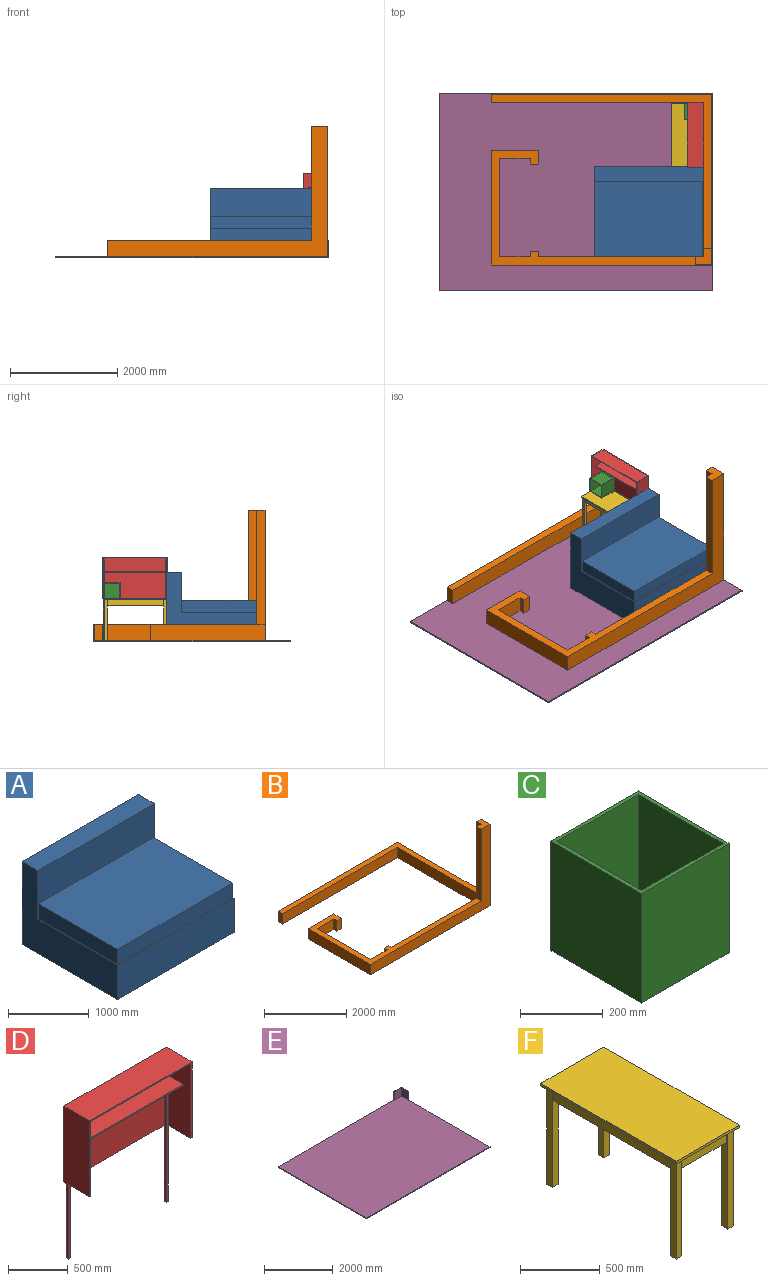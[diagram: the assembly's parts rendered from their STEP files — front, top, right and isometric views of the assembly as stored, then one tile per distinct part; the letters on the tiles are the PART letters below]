
ASSEMBLY  parts=6 mates=12
PART A: 12 faces, bbox 2038.4x1676.4x1257.3 mm
  f0: plane 1676.4x1257.3mm, normal (-1,0,0), area 1078707.5mm2, adj f1,f2,f3,f5,f6,f7
  f1: plane 2038.35x520.7mm, normal (0,-1,0), area 1061368.8mm2, adj f0,f4,f5,f6
  f2: plane 2038.35x279.4mm, normal (0,0,1), area 569515mm2, adj f0,f3,f4,f7
  f3: plane 2038.35x1257.3mm, normal (0,1,0), area 2562817.5mm2, adj f0,f2,f4,f5
  f4: plane 1676.4x1257.3mm, normal (1,0,0), area 1078707.5mm2, adj f1,f2,f3,f5,f6,f7
  f5: plane 2038.35x1676.4mm, normal (0,0,-1), area 3417089.9mm2, adj f0,f1,f3,f4
  f6: plane 2038.35x1397mm, normal (0,0,1), area 61048.3mm2, adj f0,f1,f4,f7,f8,f9,f10
  f7: plane 2038.35x736.6mm, normal (0,-1,0), area 1041288.2mm2, adj f0,f2,f4,f6,f8,f10,f11
  f8: plane 1384.3x228.6mm, normal (-1,0,0), area 316451mm2, adj f6,f7,f9,f11
  f9: plane 2012.95x228.6mm, normal (0,-1,0), area 460160.4mm2, adj f6,f8,f10,f11
  f10: plane 1384.3x228.6mm, normal (1,0,0), area 316451mm2, adj f6,f7,f9,f11
  f11: plane 2012.95x1384.3mm, normal (0,0,1), area 2786526.7mm2, adj f7,f8,f9,f10
PART B: 24 faces, bbox 4102.1x3175x2425.7 mm
  f0: plane 3797.3x2133.6mm, normal (0,0,1), area 1021933.4mm2, adj f1,f2,f3,f4,f5,f6,f7,f8
  f1: plane 304.8x101.6mm, normal (-1,0,0), area 30967.7mm2, adj f0,f2,f18,f20
  f2: plane 571.5x304.8mm, normal (0,1,0), area 174193.2mm2, adj f0,f1,f3,f20
  f3: plane 1828.8x304.8mm, normal (1,0,0), area 557418.2mm2, adj f0,f2,f4,f20
  f4: plane 571.5x304.8mm, normal (0,-1,0), area 174193.2mm2, adj f0,f3,f5,f20
  f5: plane 304.8x101.6mm, normal (-1,0,0), area 30967.7mm2, adj f0,f4,f6,f20
  f6: plane 304.8x152.4mm, normal (0,-1,0), area 46451.5mm2, adj f0,f5,f7,f20
  f7: plane 304.8x254mm, normal (1,0,0), area 77419.2mm2, adj f0,f6,f8,f20
  f8: plane 876.3x304.8mm, normal (0,1,0), area 267096.2mm2, adj f0,f7,f9,f20
  f9: plane 2133.6x304.8mm, normal (-1,0,0), area 650321.3mm2, adj f0,f8,f10,f20
  f10: plane 4102.1x2425.7mm, normal (0,-1,0), area 1896770.4mm2, adj f0,f9,f11,f20,f21,f23
  f11: plane 3175x2425.7mm, normal (1,0,0), area 1614190.3mm2, adj f10,f12,f19,f20,f22,f23
  f12: plane 4102.1x304.8mm, normal (0,1,0), area 1250320.1mm2, adj f11,f13,f19,f20
  f13: plane 304.8x152.4mm, normal (-1,0,0), area 46451.5mm2, adj f12,f14,f19,f20
  f14: plane 3949.7x304.8mm, normal (0,-1,0), area 1203868.6mm2, adj f13,f15,f19,f20
  f15: plane 2870.2x2425.7mm, normal (-1,0,0), area 1198062.1mm2, adj f14,f16,f19,f20,f22,f23
  f16: plane 3073.4x2425.7mm, normal (0,1,0), area 1259997.5mm2, adj f0,f15,f17,f20,f21,f23
  f17: plane 304.8x101.6mm, normal (1,0,0), area 30967.7mm2, adj f0,f16,f18,f20
  f18: plane 304.8x152.4mm, normal (0,1,0), area 46451.5mm2, adj f0,f1,f17,f20
  f19: plane 4102.1x2870.2mm, normal (0,0,1), area 1039352.8mm2, adj f11,f12,f13,f14,f15,f22
  f20: plane 4102.1x3175mm, normal (0,0,-1), area 2130963.5mm2, adj f1,f2,f3,f4,f5,f6,f7,f8
  f21: plane 2120.9x152.4mm, normal (-1,0,0), area 323225.2mm2, adj f0,f10,f16,f23
  f22: plane 2120.9x152.4mm, normal (0,1,0), area 323225.2mm2, adj f11,f15,f19,f23
  f23: plane 304.8x304.8mm, normal (0,0,1), area 69677.3mm2, adj f10,f11,f15,f16,f21,f22
PART C: 11 faces, bbox 298.5x311.2x323.9 mm
  f0: plane 311.15x298.45mm, normal (0,0,-1), area 92862.7mm2, adj f5,f6,f7,f8
  f1: plane 298.45x278.13mm, normal (0,-1,0), area 83007.9mm2, adj f2,f4,f9,f10
  f2: plane 298.45x290.83mm, normal (1,0,0), area 86798.2mm2, adj f1,f3,f9,f10
  f3: plane 298.45x278.13mm, normal (0,1,0), area 83007.9mm2, adj f2,f4,f9,f10
  f4: plane 298.45x290.83mm, normal (-1,0,0), area 86798.2mm2, adj f1,f3,f9,f10
  f5: plane 323.85x298.45mm, normal (0,-1,0), area 96653mm2, adj f0,f6,f8,f9
  f6: plane 323.85x311.15mm, normal (1,0,0), area 100765.9mm2, adj f0,f5,f7,f9
  f7: plane 323.85x298.45mm, normal (0,1,0), area 96653mm2, adj f0,f6,f8,f9
  f8: plane 323.85x311.15mm, normal (-1,0,0), area 100765.9mm2, adj f0,f5,f7,f9
  f9: plane 311.15x298.45mm, normal (0,0,1), area 11974.2mm2, adj f1,f2,f3,f4,f5,f6,f7,f8
  f10: plane 290.83x278.13mm, normal (0,0,1), area 80888.5mm2, adj f1,f2,f3,f4
PART D: 28 faces, bbox 1206.5x304.8x1549.4 mm
  f0: plane 1130.3x254mm, normal (0,-1,0), area 287096.2mm2, adj f13,f17,f23,f25
  f1: plane 762x266.7mm, normal (-1,0,0), area 200967.3mm2, adj f3,f11,f12,f13,f18,f25,f26,f27
  f2: plane 1270x25.4mm, normal (-1,0,0), area 32258mm2, adj f3,f7,f15,f19,f26
  f3: plane 1270x25.4mm, normal (0,-1,0), area 32258mm2, adj f1,f2,f16,f19,f26
  f4: plane 1270x25.4mm, normal (0,-1,0), area 32258mm2, adj f5,f6,f21,f24,f26
  f5: plane 1270x25.4mm, normal (1,0,0), area 32258mm2, adj f4,f7,f20,f24,f26
  f6: plane 762x266.7mm, normal (1,0,0), area 200967.3mm2, adj f4,f11,f12,f13,f22,f25,f26,f27
  f7: plane 1130.3x495.3mm, normal (0,-1,0), area 559837.6mm2, adj f2,f5,f12,f26
  f8: plane 774.7x304.8mm, normal (1,0,0), area 236128.6mm2, adj f9,f11,f12,f14
  f9: plane 1206.5x774.7mm, normal (0,1,0), area 934675.6mm2, adj f8,f10,f12,f14
  f10: plane 774.7x304.8mm, normal (-1,0,0), area 236128.6mm2, adj f9,f11,f12,f14
  f11: plane 1206.5x774.7mm, normal (0,-1,0), area 34677.4mm2, adj f1,f6,f8,f10,f12,f13,f14
  f12: plane 1206.5x304.8mm, normal (0,0,-1), area 22741.9mm2, adj f1,f6,f7,f8,f9,f10,f11,f15
  f13: plane 1181.1x292.1mm, normal (0,0,-1), area 343709mm2, adj f0,f1,f6,f11,f17,f18,f22,f23
  f14: plane 1206.5x304.8mm, normal (0,0,1), area 367741.2mm2, adj f8,f9,f10,f11
  f15: plane 774.7x25.4mm, normal (0,1,0), area 19677.4mm2, adj f2,f12,f16,f19
  f16: plane 774.7x25.4mm, normal (1,0,0), area 19677.4mm2, adj f3,f12,f15,f19
  f17: plane 254x25.4mm, normal (-1,0,0), area 6451.6mm2, adj f0,f13,f18,f25
  f18: plane 254x25.4mm, normal (0,-1,0), area 6451.6mm2, adj f1,f13,f17,f25
  f19: plane 25.4x25.4mm, normal (0,0,-1), area 645.2mm2, adj f2,f3,f15,f16
  f20: plane 774.7x25.4mm, normal (0,1,0), area 19677.4mm2, adj f5,f12,f21,f24
  f21: plane 774.7x25.4mm, normal (-1,0,0), area 19677.4mm2, adj f4,f12,f20,f24
  f22: plane 254x25.4mm, normal (0,-1,0), area 6451.6mm2, adj f6,f13,f23,f25
  f23: plane 254x25.4mm, normal (1,0,0), area 6451.6mm2, adj f0,f13,f22,f25
  f24: plane 25.4x25.4mm, normal (0,0,-1), area 645.2mm2, adj f4,f5,f20,f21
  f25: plane 1181.1x203.2mm, normal (0,0,1), area 238709.2mm2, adj f0,f1,f6,f17,f18,f22,f23,f27
  f26: plane 1181.1x203.2mm, normal (0,0,-1), area 238709.2mm2, adj f1,f2,f3,f4,f5,f6,f7,f27
  f27: plane 1181.1x12.7mm, normal (0,-1,0), area 15000mm2, adj f1,f6,f25,f26
PART E: 11 faces, bbox 5080x3657.6x330.2 mm
  f0: plane 5080x330.2mm, normal (0,1,0), area 221935mm2, adj f1,f3,f4,f5,f6,f10
  f1: plane 3657.6x25.4mm, normal (-1,0,0), area 92903mm2, adj f0,f2,f4,f5
  f2: plane 5080x25.4mm, normal (0,-1,0), area 129032mm2, adj f1,f3,f4,f5
  f3: plane 3657.6x330.2mm, normal (1,0,0), area 185806.1mm2, adj f0,f2,f4,f5,f9,f10
  f4: plane 5080x3657.6mm, normal (0,0,1), area 18573027.4mm2, adj f0,f1,f2,f3,f6,f7,f8,f9
  f5: plane 5080x3657.6mm, normal (0,0,-1), area 18580608mm2, adj f0,f1,f2,f3
  f6: plane 304.8x12.7mm, normal (-1,0,0), area 3871mm2, adj f0,f4,f7,f10
  f7: plane 304.8x292.1mm, normal (0,-1,0), area 89032.1mm2, adj f4,f6,f8,f10
  f8: plane 304.8x292.1mm, normal (-1,0,0), area 89032.1mm2, adj f4,f7,f9,f10
  f9: plane 304.8x12.7mm, normal (0,-1,0), area 3871mm2, adj f3,f4,f8,f10
  f10: plane 304.8x304.8mm, normal (0,0,1), area 7580.6mm2, adj f0,f3,f6,f7,f8,f9
PART F: 39 faces, bbox 558.8x1200.2x774.7 mm
  f0: plane 1200.15x558.8mm, normal (0,0,-1), area 123709.4mm2, adj f2,f3,f4,f5,f7,f10,f13,f16
  f1: plane 1073.15x431.8mm, normal (0,0,-1), area 462741mm2, adj f8,f11,f14,f17,f19,f22,f24,f25
  f2: plane 558.8x19.05mm, normal (0,1,0), area 10645.1mm2, adj f0,f3,f5,f6
  f3: plane 1200.15x19.05mm, normal (-1,0,0), area 22862.9mm2, adj f0,f2,f4,f6
  f4: plane 558.8x19.05mm, normal (0,-1,0), area 10645.1mm2, adj f0,f3,f5,f6
  f5: plane 1200.15x19.05mm, normal (1,0,0), area 22862.9mm2, adj f0,f2,f4,f6
  f6: plane 1200.15x558.8mm, normal (0,0,1), area 670643.8mm2, adj f2,f3,f4,f5
  f7: plane 1047.75x95.25mm, normal (-1,0,0), area 99798.2mm2, adj f0,f9,f25,f34
  f8: plane 1047.75x95.25mm, normal (1,0,0), area 99798.2mm2, adj f1,f9,f25,f34
  f9: plane 1047.75x25.4mm, normal (0,0,-1), area 26612.9mm2, adj f7,f8,f25,f34
  f10: plane 406.4x95.25mm, normal (0,-1,0), area 38709.6mm2, adj f0,f12,f22,f24
  f11: plane 406.4x95.25mm, normal (0,1,0), area 38709.6mm2, adj f1,f12,f22,f24
  f12: plane 406.4x25.4mm, normal (0,0,-1), area 10322.6mm2, adj f10,f11,f22,f24
  f13: plane 1047.75x95.25mm, normal (1,0,0), area 99798.2mm2, adj f0,f15,f19,f32
  f14: plane 1047.75x95.25mm, normal (-1,0,0), area 99798.2mm2, adj f1,f15,f19,f32
  f15: plane 1047.75x25.4mm, normal (0,0,-1), area 26612.8mm2, adj f13,f14,f19,f32
  f16: plane 406.4x95.25mm, normal (0,1,0), area 38709.6mm2, adj f0,f18,f29,f37
  f17: plane 406.4x95.25mm, normal (0,-1,0), area 38709.6mm2, adj f1,f18,f29,f37
  f18: plane 406.4x25.4mm, normal (0,0,-1), area 10322.6mm2, adj f16,f17,f29,f37
  f19: plane 755.65x50.8mm, normal (0,1,0), area 35967.7mm2, adj f0,f1,f13,f14,f15,f20,f22,f23
  f20: plane 755.65x50.8mm, normal (1,0,0), area 38387mm2, adj f0,f19,f21,f23
  f21: plane 755.65x50.8mm, normal (0,-1,0), area 38387mm2, adj f0,f20,f22,f23
  f22: plane 755.65x50.8mm, normal (-1,0,0), area 35967.7mm2, adj f0,f1,f10,f11,f12,f19,f21,f23
  f23: plane 50.8x50.8mm, normal (0,0,-1), area 2580.6mm2, adj f19,f20,f21,f22
  f24: plane 755.65x50.8mm, normal (1,0,0), area 35967.7mm2, adj f0,f1,f10,f11,f12,f25,f26,f28
  f25: plane 755.65x50.8mm, normal (0,1,0), area 35967.7mm2, adj f0,f1,f7,f8,f9,f24,f27,f28
  f26: plane 755.65x50.8mm, normal (0,-1,0), area 38387mm2, adj f0,f24,f27,f28
  f27: plane 755.65x50.8mm, normal (-1,0,0), area 38387mm2, adj f0,f25,f26,f28
  f28: plane 50.8x50.8mm, normal (0,0,-1), area 2580.6mm2, adj f24,f25,f26,f27
  f29: plane 755.65x50.8mm, normal (-1,0,0), area 35967.7mm2, adj f0,f1,f16,f17,f18,f30,f32,f33
  f30: plane 755.65x50.8mm, normal (0,1,0), area 38387mm2, adj f0,f29,f31,f33
  f31: plane 755.65x50.8mm, normal (1,0,0), area 38387mm2, adj f0,f30,f32,f33
  f32: plane 755.65x50.8mm, normal (0,-1,0), area 35967.7mm2, adj f0,f1,f13,f14,f15,f29,f31,f33
  f33: plane 50.8x50.8mm, normal (0,0,-1), area 2580.6mm2, adj f29,f30,f31,f32
  f34: plane 755.65x50.8mm, normal (0,-1,0), area 35967.7mm2, adj f0,f1,f7,f8,f9,f35,f37,f38
  f35: plane 755.65x50.8mm, normal (-1,0,0), area 38387mm2, adj f0,f34,f36,f38
  f36: plane 755.65x50.8mm, normal (0,1,0), area 38387mm2, adj f0,f35,f37,f38
  f37: plane 755.65x50.8mm, normal (1,0,0), area 35967.7mm2, adj f0,f1,f16,f17,f18,f34,f36,f38
  f38: plane 50.8x50.8mm, normal (0,0,-1), area 2580.6mm2, adj f34,f35,f36,f37
PLACE A t=(4540.57,6521.74,0)mm
PLACE B t=(-3261.73,0,0)mm
PLACE C rot(axis=(0,-1,0),90deg) t=(5430.37,7034.8,1396.97)mm
PLACE D rot(axis=(0,0,-1),90deg) t=(5577.95,6927.55,1536.7)mm
PLACE E t=(580.53,1323.05,-25.4)mm
PLACE F t=(5111.02,6469.84,755.65)mm
MATE planar C.f8 <-> F.f6  axis (0,0,-1) through (5268.44,7335.99,774.7)mm
MATE planar E.f7 <-> B.f12  axis (0,-1,0) through (5469.1,7656.66,152.4)mm
MATE planar D.f24 <-> E.f4  axis (0,0,-1) through (5437.35,7478.86,0)mm
MATE planar F.f33 <-> E.f4  axis (0,0,-1) through (5380.2,7440.76,0)mm
MATE planar F.f2 <-> D.f6  axis (0,1,0) through (5151.6,7491.56,765.18)mm
MATE planar E.f8 <-> B.f11  axis (-1,0,0) through (5615.15,7510.61,152.4)mm
MATE planar C.f7 <-> D.f6  axis (0,1,0) through (5268.44,7491.56,923.93)mm
MATE planar D.f9 <-> B.f15  axis (1,0,0) through (5462.75,6901.01,1162.05)mm
MATE planar D.f10 <-> B.f14  axis (0,1,0) through (5310.35,7504.26,1162.05)mm
MATE planar A.f4 <-> B.f15  axis (1,0,0) through (5462.75,5605.53,380.29)mm
MATE planar A.f5 <-> E.f4  axis (0,0,-1) through (4443.58,5472.26,0)mm
MATE planar A.f1 <-> B.f16  axis (0,-1,0) through (4443.58,4634.06,260.35)mm
